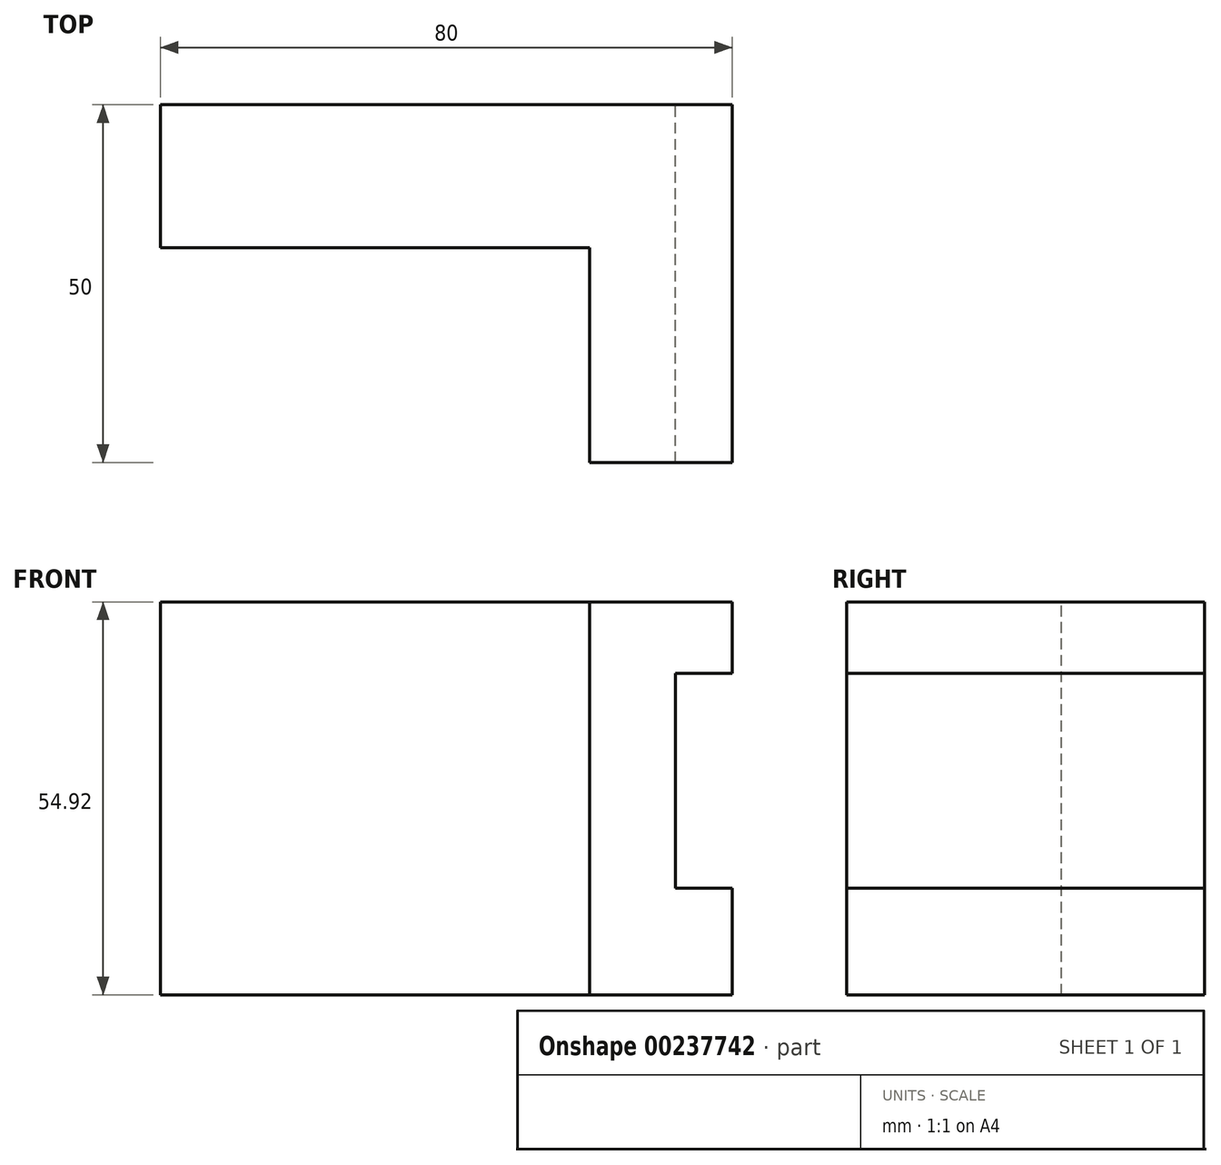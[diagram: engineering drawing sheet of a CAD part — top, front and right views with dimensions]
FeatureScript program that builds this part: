
annotation { "Feature Type Name" : "Feature", "Feature Type Description" : "" }
export const myFeature = defineFeature(function(context is Context, id is Id, definition is map)
    precondition{}
    {
        {
            var Q0;
            Q0=qCreatedBy(makeId("Front.planeOp"),FACE);
            var sketch = newSketch(context, id + "F0", { "sketchPlane" : qUnion([Q0])});
            skLineSegment(sketch, "E0", {"start": v(-60, 0) * mm, "end": v(0, 0) * mm});
            skLineSegment(sketch, "E1", {"start": v(-60, 0) * mm, "end": v(-60, 54.92) * mm});
            skLineSegment(sketch, "E2", {"start": v(-60, 54.92) * mm, "end": v(0, 54.92) * mm});
            skLineSegment(sketch, "E3", {"start": v(0, 54.92) * mm, "end": v(0, 0) * mm});
            skLineSegment(sketch, "E4", {"start": v(0, 0) * mm, "end": v(20, 0) * mm});
            skLineSegment(sketch, "E5", {"start": v(20, 0) * mm, "end": v(20, 54.92) * mm});
            skLineSegment(sketch, "E6", {"start": v(0, 54.92) * mm, "end": v(20, 54.92) * mm});
            skLineSegment(sketch, "E7", {"start": v(12, 44.92) * mm, "end": v(20, 44.92) * mm});
            skLineSegment(sketch, "E8", {"start": v(12, 44.92) * mm, "end": v(12, 14.92) * mm});
            skLineSegment(sketch, "E9", {"start": v(12, 14.92) * mm, "end": v(20, 14.92) * mm});
            skSolve(sketch);
        }
        {
            var Q0;
            Q0=makeQuery(id+"F0.imprint","IMPRINT",FACE,{"disambiguationData":[TD([[makeQuery(id+"F0.imprint","IMPRINT",EDGE,{"derivedFrom":sQuery(id+"F0.wireOp",EDGE,"E0")}),1.0]])]});
            extrude(context, id + "F1", {"entities" : qUnion([Q0]), "depth" : 20 * mm});
        }
        {
            var Q0;
            Q0=makeQuery(id+"F0.imprint","IMPRINT",FACE,{"disambiguationData":[TD([[makeQuery(id+"F0.imprint","IMPRINT",EDGE,{"derivedFrom":sQuery(id+"F0.wireOp",EDGE,"E3")}),1.0]])]});
            extrude(context, id + "F2", {"entities" : qUnion([Q0]), "operationType" : NewBodyOperationType.ADD, "depth" : 50 * mm});
        }
    });
